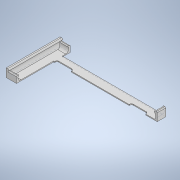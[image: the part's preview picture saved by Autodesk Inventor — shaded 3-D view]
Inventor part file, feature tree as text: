
AUTODESK INVENTOR PART (.ipt)
format: ipt  version: 2020 (Build 240168000, 168)  size: 333,312 bytes
history: native  units: in
note: dims shown in document units (in); Inventor stores cm internally (conversion verified against a paired STEP export)
features: other x3, sketch x3, projected_geometry x2, extrude x1
ambient origin geometry x8: Origin, YZ Plane, XZ Plane, XY Plane, X Axis, Y Axis, Z Axis, Center Point
bodies: Solid1 (feature_tree)
feature tree (9):
  other  "Part9 scaled.ipt"
  extrude  "Extrusion1"  TaperAngle=0.0deg  [1 undecoded]
  other  "Solid1::Part9 scaled.ipt"
  other  "TaggingFeature1"
  sketch  "Sketch22"
  sketch  "Sketch23"
  sketch  "Sketch3"  dims[d0=0.3937in d1=0.0in d2=0.0in]
  projected_geometry  "Projected Loop1"
  projected_geometry  "Projected Loop2"
note: 1 required parameter value undecoded (feature->parameter linkage not recoverable at this tier; creation-order binding heuristic only, values carry confidence <= 0.55)
